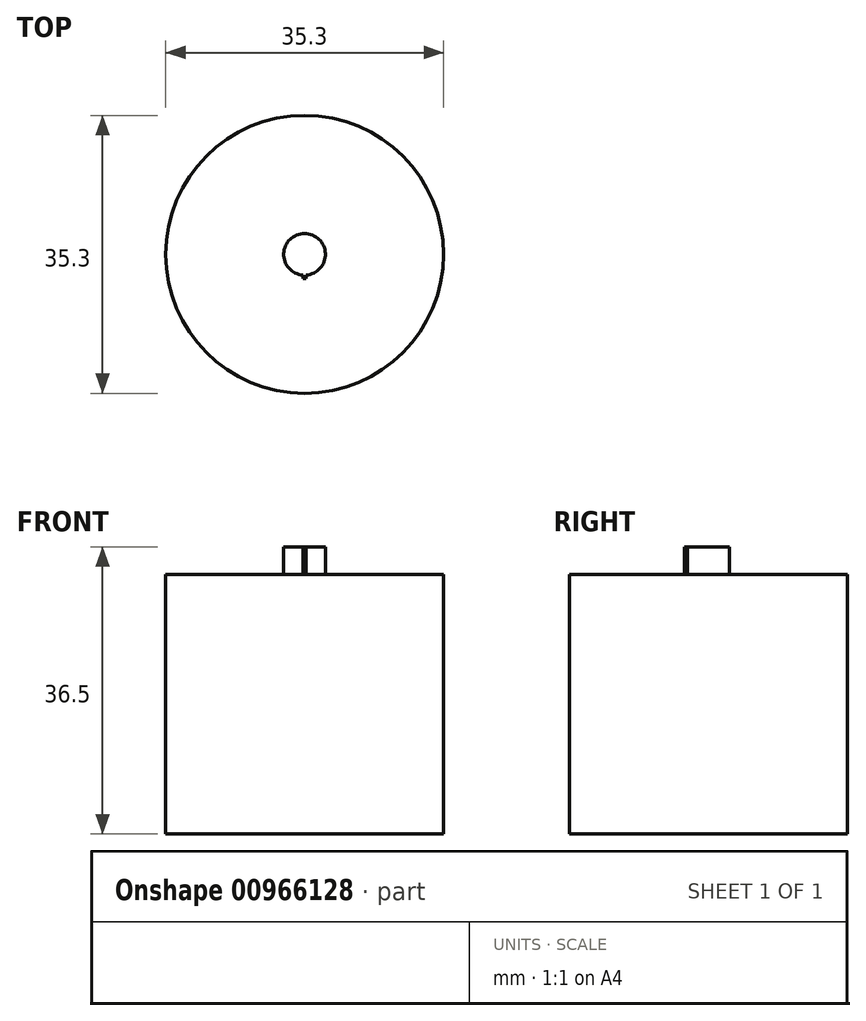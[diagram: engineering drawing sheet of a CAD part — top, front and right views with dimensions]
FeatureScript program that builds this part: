
annotation { "Feature Type Name" : "Feature", "Feature Type Description" : "" }
export const myFeature = defineFeature(function(context is Context, id is Id, definition is map)
    precondition{}
    {
        {
            var Q0;
            Q0=qCreatedBy(makeId("Top.planeOp"),FACE);
            var sketch = newSketch(context, id + "F0", { "sketchPlane" : qUnion([Q0])});
            skCircle(sketch, "E0", {"center": v(0, 0) * mm, "radius": 17.65 * mm});
            skSolve(sketch);
        }
        {
            var Q0;
            Q0=makeQuery(id+"F0.imprint","IMPRINT",FACE,{"disambiguationData":[TD([[makeQuery(id+"F0.imprint","IMPRINT",EDGE,{"derivedFrom":sQuery(id+"F0.wireOp",EDGE,"E0")}),1.0]])]});
            extrude(context, id + "F1", {"entities" : qUnion([Q0]), "depth" : 33 * mm, "offsetDistance" : 25 * mm});
        }
        {
            var Q0;
            Q0=makeQuery(id+"F1.opExtrude","CAP_FACE",FACE,{"disambiguationData":[OSD([sQuery(id+"F0.wireOp",EDGE,"E0")])],"isStart":false});
            var sketch = newSketch(context, id + "F2", { "sketchPlane" : qUnion([Q0])});
            skCircle(sketch, "E1", {"center": v(0, 0) * mm, "radius": 2.65 * mm});
            skSolve(sketch);
        }
        {
            var Q0;
            Q0 = qSketchRegion(id + "F2", true);
            extrude(context, id + "F3", {"entities" : qUnion([Q0]), "operationType" : NewBodyOperationType.ADD, "depth" : 3.5 * mm, "offsetDistance" : 25 * mm});
        }
        {
            var Q0;
            Q0=makeQuery(id+"F1.opExtrude","CAP_FACE",FACE,{"disambiguationData":[OSD([sQuery(id+"F0.wireOp",EDGE,"E0")])],"isStart":false});
            var sketch = newSketch(context, id + "F4", { "sketchPlane" : qUnion([Q0])});
            skLineSegment(sketch, "E2.bottom", {"start": v(0, -2.65) * mm, "end": v(0, -2.65) * mm});
            skLineSegment(sketch, "E2.top", {"start": v(0, -3.05) * mm, "end": v(0, -3.05) * mm});
            skLineSegment(sketch, "E2.left", {"start": v(0, -2.65) * mm, "end": v(0, -3.05) * mm, "construction": true});
            skLineSegment(sketch, "E2.right", {"start": v(0, -2.65) * mm, "end": v(0, -3.05) * mm, "construction": true});
            skLineSegment(sketch, "E3", {"start": v(-0.2, -2.64) * mm, "end": v(-0.2, -3.04) * mm});
            skLineSegment(sketch, "E4", {"start": v(-0.2, -3.04) * mm, "end": v(0, -3.04) * mm});
            skLineSegment(sketch, "E5", {"start": v(0, -3.04) * mm, "end": v(0.2, -3.04) * mm});
            skLineSegment(sketch, "E6", {"start": v(0.2, -3.04) * mm, "end": v(0.2, -2.64) * mm});
            skSolve(sketch);
        }
        {
            var Q0;
            {var subQ1=sQuery(id+"F4.wireOp",EDGE,"E3");Q0=makeQuery(id+"F4.imprint","IMPRINT",FACE,{"disambiguationData":[TD([[makeQuery(id+"F4.imprint","IMPRINT",EDGE,{"derivedFrom":subQ1}),1.0]])]});}
            extrude(context, id + "F5", {"entities" : qUnion([Q0]), "operationType" : NewBodyOperationType.ADD, "depth" : 3.5 * mm, "offsetDistance" : 25 * mm});
        }
    });
